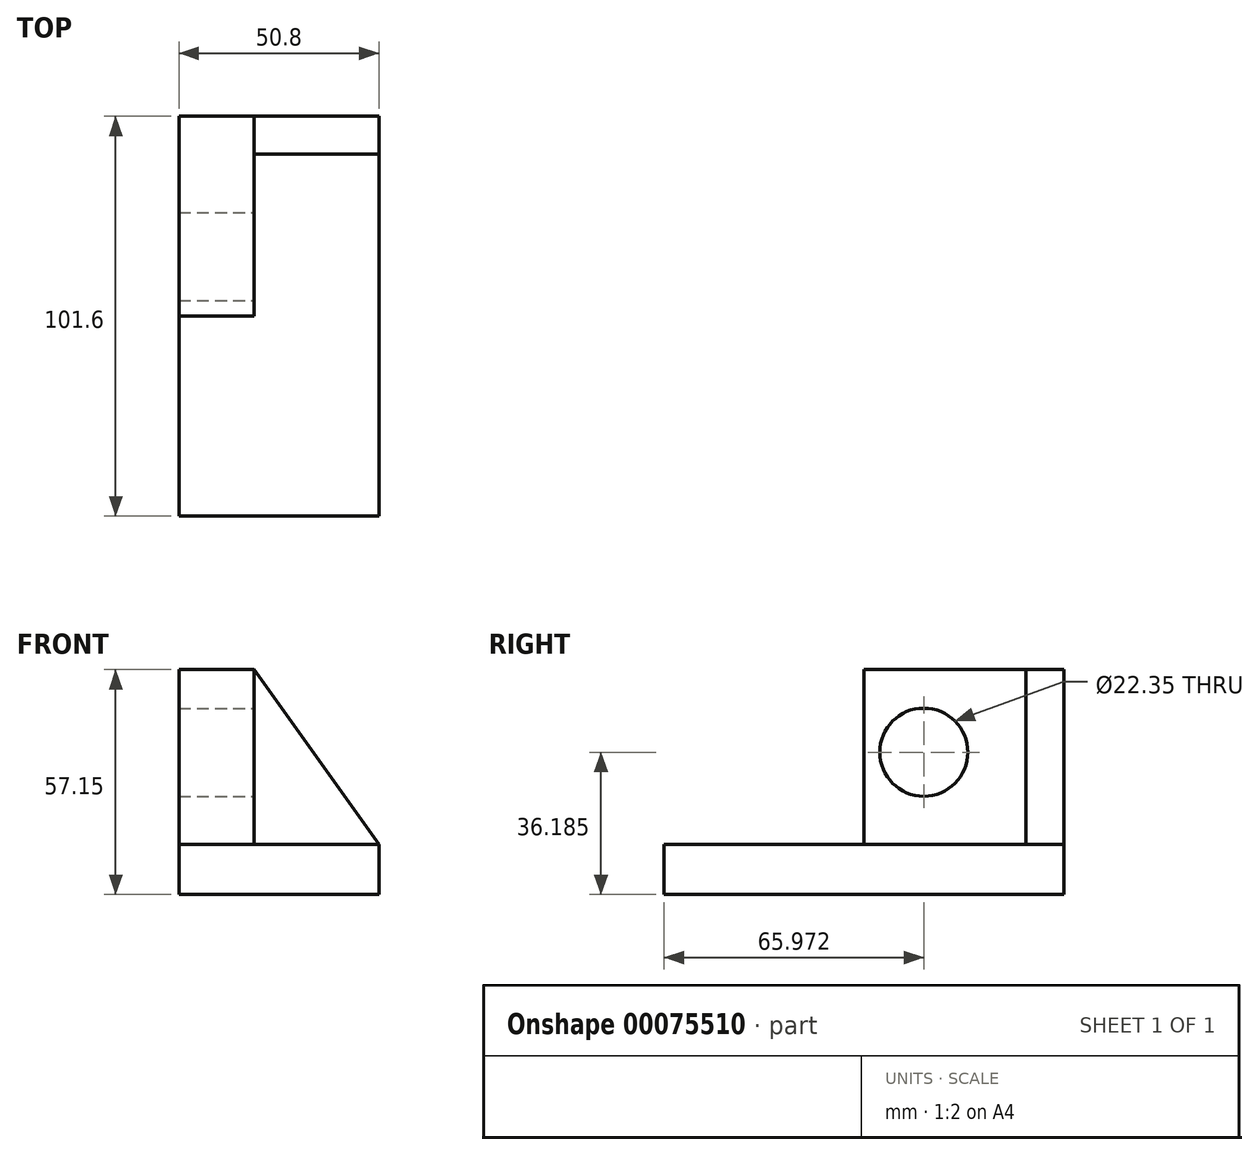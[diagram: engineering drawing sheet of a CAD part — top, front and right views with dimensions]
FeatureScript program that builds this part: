
annotation { "Feature Type Name" : "Feature", "Feature Type Description" : "" }
export const myFeature = defineFeature(function(context is Context, id is Id, definition is map)
    precondition{}
    {
        {
            var Q0;
            Q0=qCreatedBy(makeId("Top.planeOp"),FACE);
            var sketch = newSketch(context, id + "F0", { "sketchPlane" : qUnion([Q0])});
            skLineSegment(sketch, "E0", {"start": v(-25.27, -101.6) * mm, "end": v(25.53, -101.6) * mm});
            skLineSegment(sketch, "E1", {"start": v(25.53, -101.6) * mm, "end": v(25.53, 0) * mm});
            skLineSegment(sketch, "E2", {"start": v(25.53, 0) * mm, "end": v(-25.27, 0) * mm});
            skLineSegment(sketch, "E3", {"start": v(-25.27, 0) * mm, "end": v(-25.27, -101.6) * mm});
            skSolve(sketch);
        }
        {
            var Q0;
            Q0=makeQuery(id+"F0.imprint","IMPRINT",FACE,{"disambiguationData":[TD([[makeQuery(id+"F0.imprint","IMPRINT",EDGE,{"derivedFrom":sQuery(id+"F0.wireOp",EDGE,"E0")}),1.0]])]});
            extrude(context, id + "F1", {"entities" : qUnion([Q0]), "depth" : 12.7 * mm});
        }
        {
            var Q0;
            Q0=makeQuery(id+"F1.opExtrude","CAP_FACE",FACE,{"disambiguationData":[OSD([sQuery(id+"F0.wireOp",EDGE,"E0"),sQuery(id+"F0.wireOp",EDGE,"E1"),sQuery(id+"F0.wireOp",EDGE,"E2"),sQuery(id+"F0.wireOp",EDGE,"E3")])],"isStart":false});
            var sketch = newSketch(context, id + "F2", { "sketchPlane" : qUnion([Q0])});
            skLineSegment(sketch, "E4.bottom", {"start": v(-25.27, 0) * mm, "end": v(-6.22, 0) * mm});
            skLineSegment(sketch, "E4.top", {"start": v(-25.27, -50.8) * mm, "end": v(-6.22, -50.8) * mm});
            skLineSegment(sketch, "E4.left", {"start": v(-25.27, 0) * mm, "end": v(-25.27, -50.8) * mm});
            skLineSegment(sketch, "E4.right", {"start": v(-6.22, 0) * mm, "end": v(-6.22, -50.8) * mm});
            skSolve(sketch);
        }
        {
            var Q0;
            Q0 = qSketchRegion(id + "F2", true);
            extrude(context, id + "F3", {"entities" : qUnion([Q0]), "operationType" : NewBodyOperationType.ADD, "depth" : 44.45 * mm});
        }
        {
            var Q0;
            Q0=makeQuery(id+"F3.boolean.opBoolean","MERGE",FACE,{"derivedFrom":[makeQuery(id+"F1.opExtrude","SWEPT_FACE",FACE,{"disambiguationData":[OSD([sQuery(id+"F0.wireOp",EDGE,"E2")])]}),makeQuery(id+"F3.opExtrude","SWEPT_FACE",FACE,{"disambiguationData":[OSD([sQuery(id+"F2.wireOp",EDGE,"E4.bottom")])]})]});
            var sketch = newSketch(context, id + "F4", { "sketchPlane" : qUnion([Q0])});
            skLineSegment(sketch, "E5", {"start": v(6.22, 57.15) * mm, "end": v(-25.53, 12.7) * mm});
            skLineSegment(sketch, "E6", {"start": v(-25.53, 12.7) * mm, "end": v(6.22, 12.7) * mm});
            skLineSegment(sketch, "E7", {"start": v(6.22, 12.7) * mm, "end": v(6.22, 57.15) * mm});
            skSolve(sketch);
        }
        {
            var Q0;
            Q0 = qSketchRegion(id + "F4", true);
            extrude(context, id + "F5", {"entities" : qUnion([Q0]), "operationType" : NewBodyOperationType.ADD, "oppositeDirection" : true, "depth" : 9.65 * mm});
        }
        {
            var Q0;
            Q0=makeQuery(id+"F3.opExtrude","SWEPT_FACE",FACE,{"disambiguationData":[OSD([sQuery(id+"F2.wireOp",EDGE,"E4.right")])]});
            var sketch = newSketch(context, id + "F6", { "sketchPlane" : qUnion([Q0])});
            skCircle(sketch, "E8", {"center": v(-35.63, 36.18) * mm, "radius": 11.18 * mm});
            skSolve(sketch);
        }
        {
            var Q0;
            Q0=sQuery(id+"F6.wireOp",VERTEX,"E8.center");
            var Q1;
            Q1=makeQuery(id+"F1.opExtrude","SWEPT_BODY",BODY,{"disambiguationData":[OSD([sQuery(id+"F0.wireOp",EDGE,"E0"),sQuery(id+"F0.wireOp",EDGE,"E1"),sQuery(id+"F0.wireOp",EDGE,"E2"),sQuery(id+"F0.wireOp",EDGE,"E3")])]});
            hole(context, id + "F7", {"style" : HoleStyle.SIMPLE, "endStyle" : HoleEndStyle.THROUGH, "holeDiameter" : 22.35 * mm, "locations" : qUnion([Q0]), "scope" : qUnion([Q1]), "isTappedThrough" : true});
        }
    });
